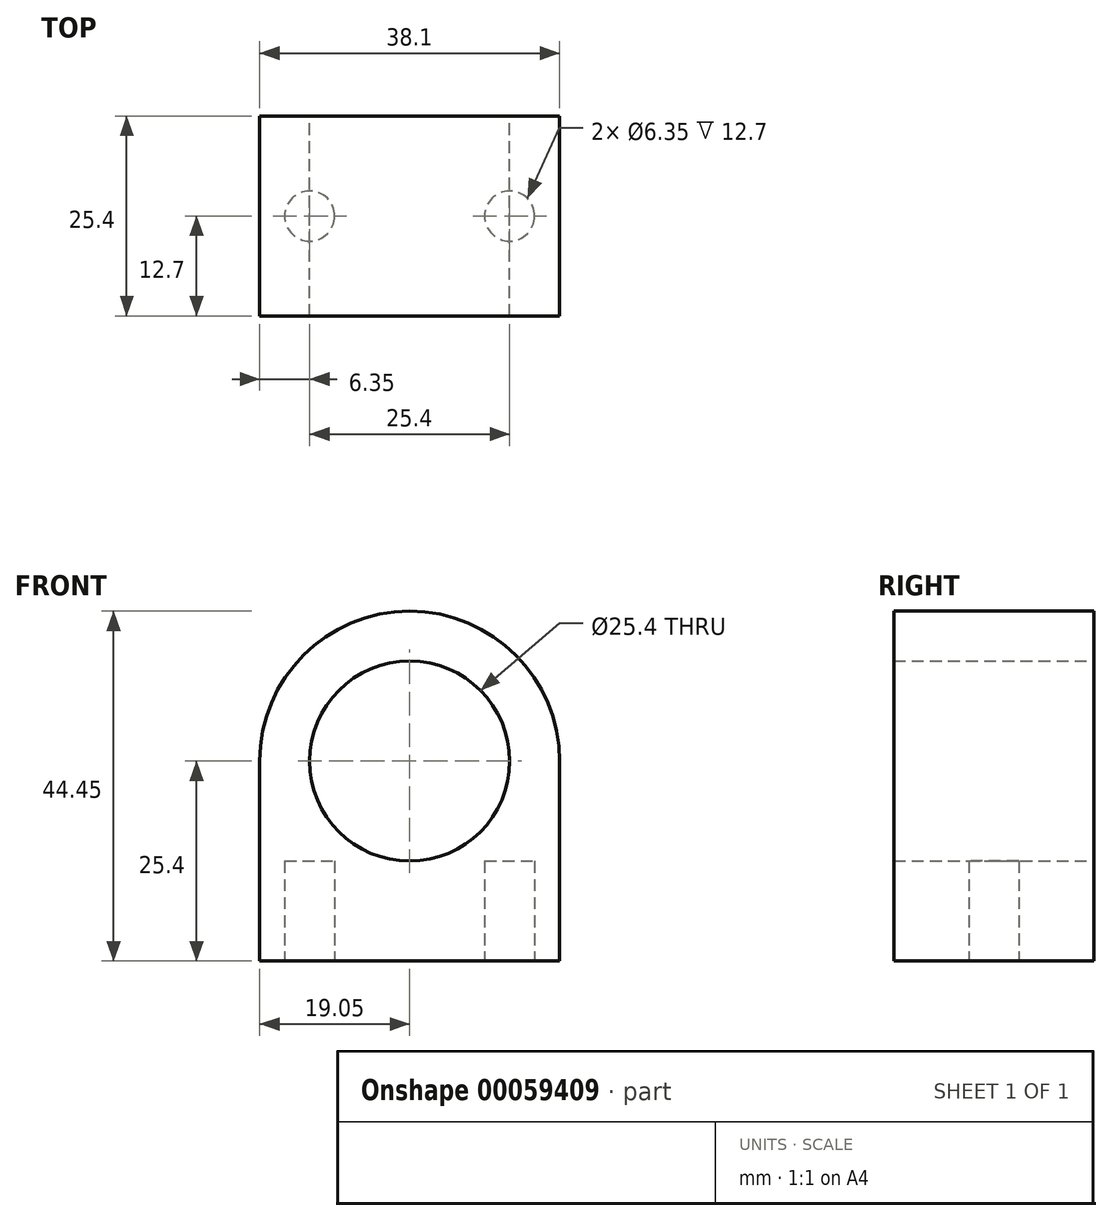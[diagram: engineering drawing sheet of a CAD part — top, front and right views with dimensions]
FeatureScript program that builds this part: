
annotation { "Feature Type Name" : "Feature", "Feature Type Description" : "" }
export const myFeature = defineFeature(function(context is Context, id is Id, definition is map)
    precondition{}
    {
        {
            var Q0;
            Q0=qCreatedBy(makeId("Front.planeOp"),FACE);
            var sketch = newSketch(context, id + "F0", { "sketchPlane" : qUnion([Q0])});
            skCircle(sketch, "E0", {"center": v(0, 0) * mm, "radius": 12.7 * mm});
            skArc(sketch, "E1", {"start": v(19.05, 0) * mm, "mid": v(0, 19.05) * mm, "end": v(-19.05, 0) * mm});
            skLineSegment(sketch, "E2", {"start": v(-19.05, 0) * mm, "end": v(-19.05, -25.4) * mm});
            skLineSegment(sketch, "E3", {"start": v(-19.05, -25.4) * mm, "end": v(19.05, -25.4) * mm});
            skLineSegment(sketch, "E4", {"start": v(19.05, 0) * mm, "end": v(19.05, -25.4) * mm});
            skSolve(sketch);
        }
        {
            var Q0;
            Q0=qSketchRegion(id+"F0",true);
            extrude(context, id + "F1", {"entities" : qUnion([Q0]), "endBound" : BoundingType.SYMMETRIC, "depth" : 25.4 * mm});
        }
        {
            var Q0;
            Q0=makeQuery(id+"F1.opExtrude","SWEPT_FACE",FACE,{"disambiguationData":[OSD([sQuery(id+"F0.wireOp",EDGE,"E3")])]});
            var sketch = newSketch(context, id + "F2", { "sketchPlane" : qUnion([Q0])});
            skCircle(sketch, "E5", {"center": v(-12.7, 0) * mm, "radius": 3.18 * mm});
            skCircle(sketch, "E6", {"center": v(12.7, 0) * mm, "radius": 3.18 * mm});
            skSolve(sketch);
        }
        {
            var Q0;
            Q0=qSketchRegion(id+"F2",true);
            extrude(context, id + "F3", {"entities" : qUnion([Q0]), "operationType" : NewBodyOperationType.REMOVE, "oppositeDirection" : true, "depth" : 12.7 * mm});
        }
    });
